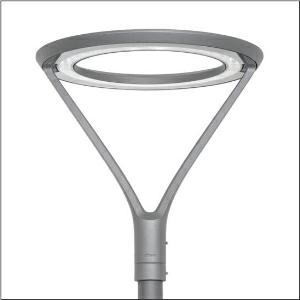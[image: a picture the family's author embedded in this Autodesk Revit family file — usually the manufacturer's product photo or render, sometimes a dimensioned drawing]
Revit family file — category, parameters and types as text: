
# Revit family: dl_20___pl1_2s_5xa512836s008p_5a13
name_source: partatom
category: Lighting Fixtures
units: mm (PartAtom-declared; Revit-internal decimal feet)

## family parameters
Cut with Voids When Loaded = No
Host = Face
Light Source = No
Part Type = Normal
Room Calculation Point = No
Round Connector Dimension = Use Diameter
Shared = No

## types (1)
- --- (1 x LED, 4250 lm, 40.6 W, 2700K)
    Apparent Load = 41 VA
    CIE Flux Codes = 33 78 99 100 100
    Color Rendering = 70
    Color Temperature = 2700K
    Default Elevation = 1800 mm
    Description = DL® 20, mast luminaire, primary light control with reflector, highly specular, primary optical cover: cover, of toughened safety glass of clear glass with excellent transmission level, light distribution: PL1.2s, light emission: direct distribution, primary light characteristic: symmetric, installation type: post-top, LED, High Power LED, rated luminous flux: 4.250lm, luminous efficacy: 105lm/W, light colour: 727, colour temperature: 2700K, control gear: Plus, control: flexible luminous flux parameterisation, time-dependent luminous flux control, constant luminous flux control, digital communication interface, power reduction, overheat protection, electronic power reduction, mains connection: 220..240V, 50/60Hz, connection cable pre-assembled, cable length: 5m, start of lifetime: 41W, end of service life: 42W, reduction: 20W, luminaire housing, upper part, of cast aluminium, powder-coated, Siteco® metallic grey (DB 702S), diameter: 690mm, height: 690mm, spigot size: 76mm (post-top), mounting height: 4..6m, luminaire housing, of cast aluminium, powder-coated, Siteco® metallic grey (DB 702S), equipment: Power, protection rating (complete): IP66, insulation class (complete): insulation class II (safety insulation), certification: CE, ENEC, VDE, impact resistance: IK08, permissible operating ambient temperature: -25..+30°C, standard-compliant lighting for roads and squares, packaging unit: 1 piece

Light Distribution: PL1.2s
    Height = 690 mm
    Lamp = 1 x LED
    Lamp Light Flux = 4250 lm
    Lamp Power = 40.6 W
    Lamp count = 1
    Length = 690 mm
    Luminous efficacy = 105 lm/W
    Manufacturer = Siteco
    ModVariant = No
    Model = 5XA512836S008P
    Mounting Place = Pole
    Mounting Type = Pole top
    Number of Poles = 1
    OnlyDefault = Yes
    Power Factor = 1
    Product Name = DL 20 | PL1.2s
    Product group = mast luminaire | pylon top
    ProductGroupID = 6100
    Protection Class = Protection class II
    Protection Degree = IP 66
    RLX_Detail_Level = 1
    RLX_Emergency_Light_Flux = 0 lm
    RLX_Emergency_Type = 0
    RLX_Emergency_Type_DB = No
    RlxData = <blob elided: 204821 chars, md5=80f37e55>
    Socket = socket
    Standby Power = 0 W
    System Light Flux = 4250 lm
    System Power = 41 W
    Type Comments = factory setting: luminous flux: 100 % | dim-lin: 254 | 549 mA
    Type Image = l_1006001.jpg
    URL = http://relux.com
    VarID = @adj_086079
    Voltage = 0 V
    Weight = 0.00 kg
    Width = 0 mm  [stored 0 ft]

note: [stored X ft] marks values corroborated as IEEE doubles in the binary element streams (Revit-internal decimal feet)

## geometry (parser evidence)
native form markers: Blend x4, Sweep x11
no freeform markers — native parametric forms only
